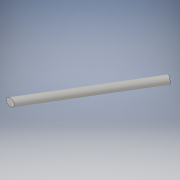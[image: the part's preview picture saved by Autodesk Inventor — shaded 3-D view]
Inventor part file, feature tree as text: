
AUTODESK INVENTOR PART (.ipt)
format: ipt  version: 2016 (Build 200138000, 138)  size: 101,376 bytes
history: native  units: in
note: dims shown in document units (in); Inventor stores cm internally (conversion verified against a paired STEP export)
features: extrude x2, sketch x2
ambient origin geometry x8: Origin, YZ Plane, XZ Plane, XY Plane, X Axis, Y Axis, Z Axis, Center Point
bodies: Solid1 (feature_tree)
feature tree (4):
  extrude  "Extrusion1"  Depth=11.66in
  extrude  "Extrusion2"  Depth=0.75in TaperAngle=0.0deg
  sketch  "Sketch2"  dims[d9=11.66in d12=0.4054in]
  sketch  "Sketch3"  dims[d13=0.75in d15=0.75in d16=0.0in d18=0.75in d19=0.75in d20=0.0in]
